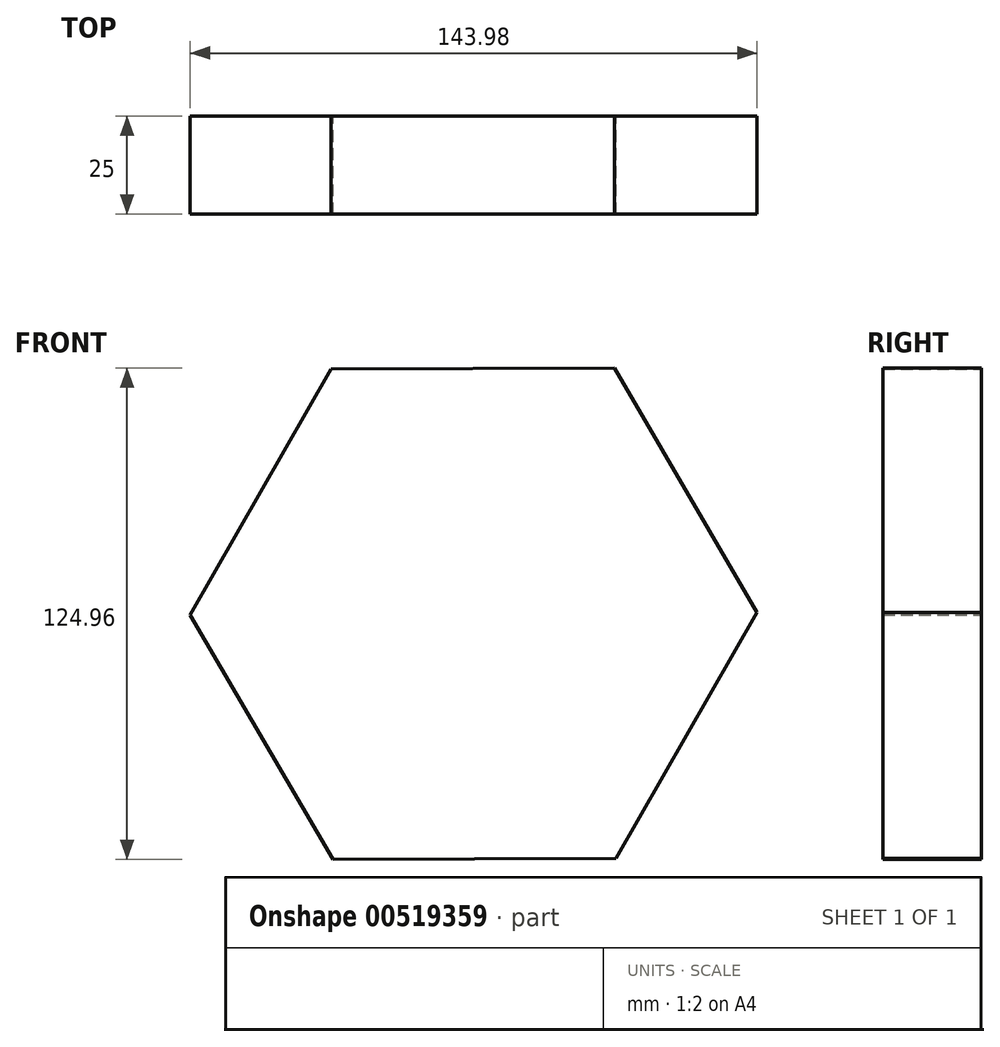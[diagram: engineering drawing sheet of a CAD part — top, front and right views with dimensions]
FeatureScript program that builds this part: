
annotation { "Feature Type Name" : "Feature", "Feature Type Description" : "" }
export const myFeature = defineFeature(function(context is Context, id is Id, definition is map)
    precondition{}
    {
        {
            var Q0;
            Q0=qCreatedBy(makeId("Front.planeOp"),FACE);
            var sketch = newSketch(context, id + "F0", { "sketchPlane" : qUnion([Q0])});
            skCircle(sketch, "E0.cCircle", {"center": v(0, 0) * mm, "radius": 62.34 * mm, "construction": true});
            skLineSegment(sketch, "E0.0", {"start": v(-71.99, -0.28) * mm, "end": v(-36.24, 62.2) * mm});
            skLineSegment(sketch, "E0.1", {"start": v(-36.24, 62.2) * mm, "end": v(35.75, 62.48) * mm});
            skLineSegment(sketch, "E0.2", {"start": v(35.75, 62.48) * mm, "end": v(71.99, 0.28) * mm});
            skLineSegment(sketch, "E0.3", {"start": v(71.99, 0.28) * mm, "end": v(36.24, -62.2) * mm});
            skLineSegment(sketch, "E0.4", {"start": v(36.24, -62.2) * mm, "end": v(-35.75, -62.48) * mm});
            skLineSegment(sketch, "E0.5", {"start": v(-35.75, -62.48) * mm, "end": v(-71.99, -0.28) * mm});
            skPoint(sketch, "E0.0.midPoint", {"position": v(-54.11, 30.96) * mm});
            skSolve(sketch);
        }
        {
            var Q0;
            Q0=makeQuery(id+"F0.imprint","IMPRINT",FACE,{"disambiguationData":[TD([[makeQuery(id+"F0.imprint","IMPRINT",EDGE,{"derivedFrom":sQuery(id+"F0.wireOp",EDGE,"E0.0")}),-1.0]])]});
            extrude(context, id + "F1", {"entities" : qUnion([Q0]), "depth" : 25 * mm, "offsetDistance" : 25 * mm});
        }
    });
